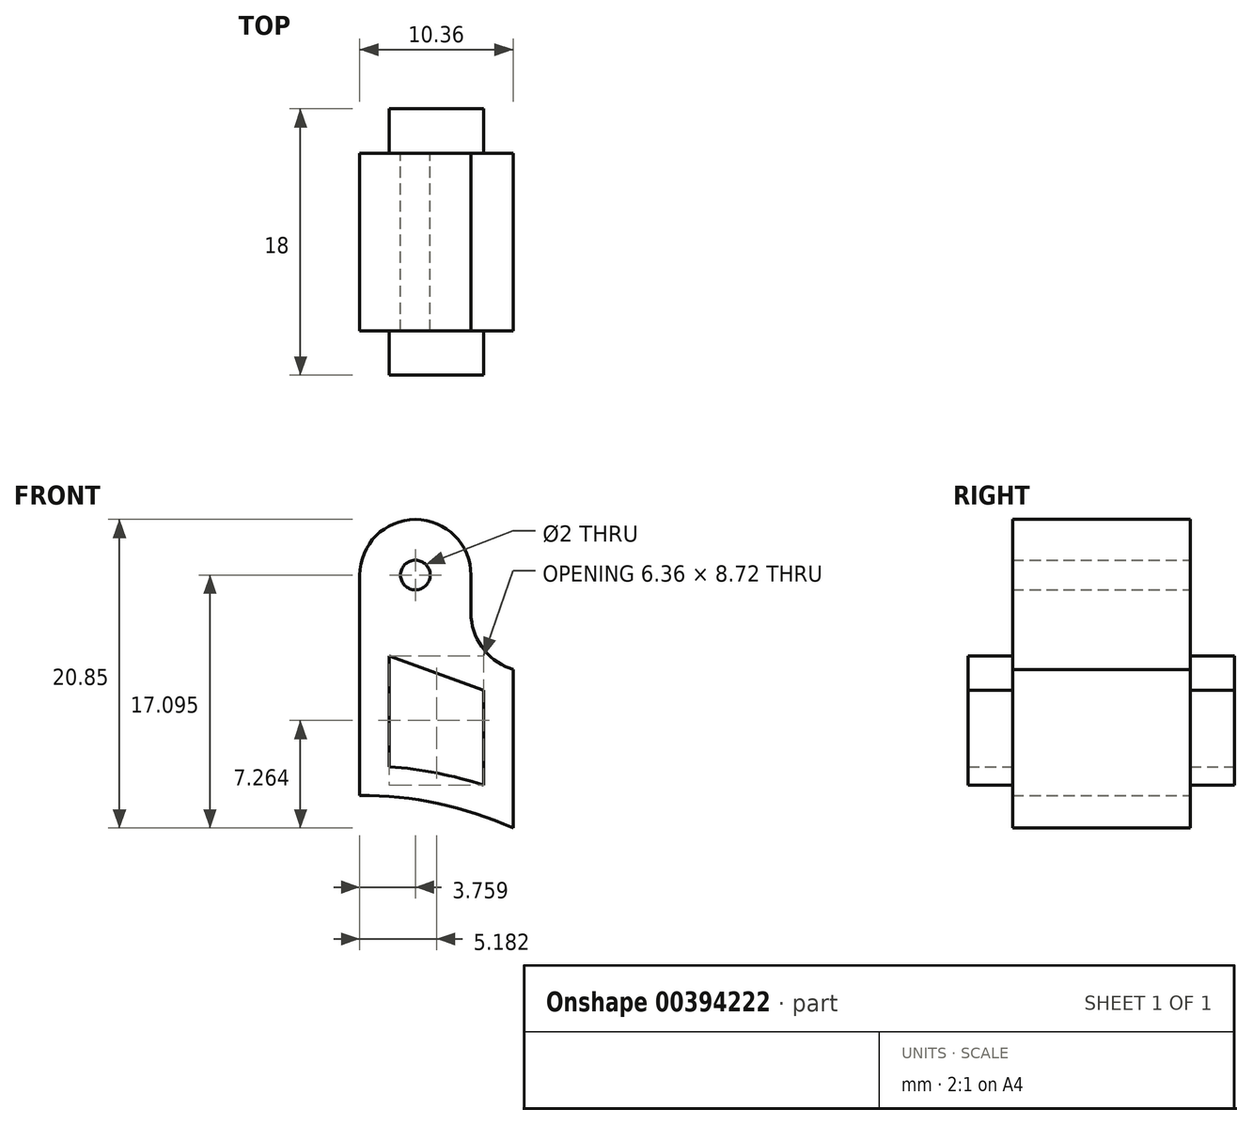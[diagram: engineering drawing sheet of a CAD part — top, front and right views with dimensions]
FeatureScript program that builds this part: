
annotation { "Feature Type Name" : "Feature", "Feature Type Description" : "" }
export const myFeature = defineFeature(function(context is Context, id is Id, definition is map)
    precondition{}
    {
        {
            var Q0;
            Q0=qCreatedBy(makeId("Front.planeOp"),FACE);
            var sketch = newSketch(context, id + "F0", { "sketchPlane" : qUnion([Q0])});
            skLineSegment(sketch, "E0.5", {"start": v(2, 34.82) * mm, "end": v(8.36, 32.5) * mm});
            skLineSegment(sketch, "E1", {"start": v(0, 25.4) * mm, "end": v(0, 37.67) * mm});
            skArc(sketch, "E2.trimOffspring", {"start": v(8.36, 26.1) * mm, "mid": v(5.22, 26.9) * mm, "end": v(2, 27.33) * mm});
            skLineSegment(sketch, "E3", {"start": v(2, 34.82) * mm, "end": v(2, 27.33) * mm});
            skLineSegment(sketch, "E4", {"start": v(10.36, 25.36) * mm, "end": v(10.36, 23.19) * mm});
            skLineSegment(sketch, "E5", {"start": v(10.36, 25.36) * mm, "end": v(10.36, 33.9) * mm});
            skArc(sketch, "E6.trimOffspring", {"start": v(10.36, 23.19) * mm, "mid": v(5.3, 24.84) * mm, "end": v(0, 25.4) * mm});
            skLineSegment(sketch, "E7", {"start": v(8.36, 32.5) * mm, "end": v(8.36, 26.1) * mm});
            skLineSegment(sketch, "E8", {"start": v(0, 37.67) * mm, "end": v(0, 40.28) * mm});
            skLineSegment(sketch, "E9", {"start": v(7.52, 40.28) * mm, "end": v(7.52, 34.94) * mm});
            skArc(sketch, "E10", {"start": v(7.52, 40.28) * mm, "mid": v(3.76, 44.04) * mm, "end": v(0, 40.28) * mm});
            skPoint(sketch, "E11.start.orphan", {"position": v(3.76, 36.3) * mm});
            skLineSegment(sketch, "E12.trimOffspring", {"start": v(7.52, 34.94) * mm, "end": v(10.36, 33.9) * mm});
            skLineSegment(sketch, "E13", {"start": v(0, 37.67) * mm, "end": v(7.52, 34.94) * mm});
            skCircle(sketch, "E14", {"center": v(3.76, 40.28) * mm, "radius": 1 * mm});
            skSolve(sketch);
        }
        {
            var Q0;
            Q0=makeQuery(id+"F0.imprint","IMPRINT",FACE,{"disambiguationData":[TD([[makeQuery(id+"F0.imprint","IMPRINT",EDGE,{"derivedFrom":sQuery(id+"F0.wireOp",EDGE,"E0.5")}),1.0]])]});
            var Q1;
            Q1=makeQuery(id+"F0.imprint","IMPRINT",FACE,{"disambiguationData":[TD([[makeQuery(id+"F0.imprint","IMPRINT",EDGE,{"derivedFrom":sQuery(id+"F0.wireOp",EDGE,"E8")}),-1.0]])]});
            extrude(context, id + "F1", {"entities" : qUnion([Q0, Q1]), "endBound" : BoundingType.SYMMETRIC, "depth" : 12 * mm});
        }
        {
            var Q0;
            Q0=makeQuery(id+"F0.imprint","IMPRINT",FACE,{"disambiguationData":[TD([[makeQuery(id+"F0.imprint","IMPRINT",EDGE,{"derivedFrom":sQuery(id+"F0.wireOp",EDGE,"E0.5")}),-1.0]])]});
            extrude(context, id + "F2", {"entities" : qUnion([Q0]), "operationType" : NewBodyOperationType.ADD, "endBound" : BoundingType.SYMMETRIC, "depth" : 18 * mm});
        }
        {
            var Q0;
            Q0=makeQuery(id+"F1.opExtrude","SWEPT_EDGE",EDGE,{"disambiguationData":[OSD([sQuery(id+"F0.wireOp",EDGE,"E9"),sQuery(id+"F0.wireOp",EDGE,"E12.trimOffspring"),sQuery(id+"F0.wireOp",EDGE,"E13")])]});
            fillet(context, id + "F3", {"entities" : qUnion([Q0]), "radius" : 4 * mm, "tangentPropagation" : true, "allowEdgeOverflow" : false});
        }
    });
